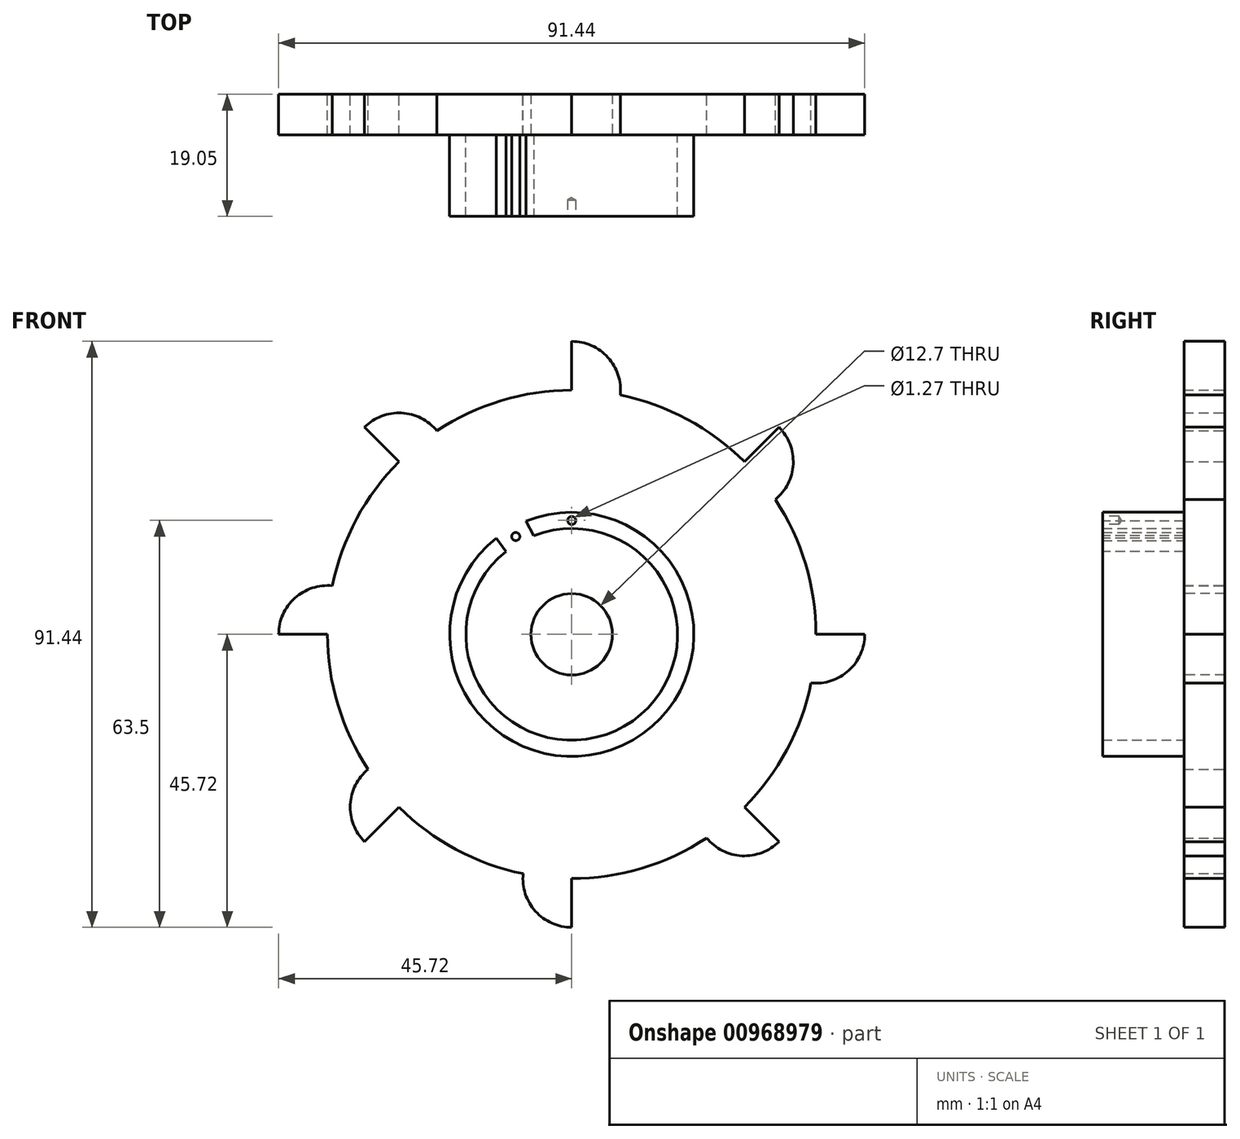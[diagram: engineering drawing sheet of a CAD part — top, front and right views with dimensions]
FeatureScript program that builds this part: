
annotation { "Feature Type Name" : "Feature", "Feature Type Description" : "" }
export const myFeature = defineFeature(function(context is Context, id is Id, definition is map)
    precondition{}
    {
        {
            var Q0;
            Q0=qCreatedBy(makeId("Front.planeOp"),FACE);
            var sketch = newSketch(context, id + "F0", { "sketchPlane" : qUnion([Q0])});
            skCircle(sketch, "E0", {"center": v(0, 0) * mm, "radius": 38.1 * mm});
            skLineSegment(sketch, "E1", {"start": v(0, 0) * mm, "end": v(0, 38.1) * mm});
            skLineSegment(sketch, "E2", {"start": v(0, 38.1) * mm, "end": v(0, 45.72) * mm});
            skArc(sketch, "E3", {"start": v(0, 45.72) * mm, "mid": v(5.65, 43.21) * mm, "end": v(7.58, 37.34) * mm});
            skArc(sketch, "E4.1.0", {"start": v(-32.33, 32.33) * mm, "mid": v(-26.56, 34.55) * mm, "end": v(-21.04, 31.76) * mm});
            skLineSegment(sketch, "E4.1.1", {"start": v(-26.94, 26.94) * mm, "end": v(-32.33, 32.33) * mm});
            skArc(sketch, "E4.2.0", {"start": v(-45.72, 0) * mm, "mid": v(-43.21, 5.65) * mm, "end": v(-37.34, 7.58) * mm});
            skLineSegment(sketch, "E4.2.1", {"start": v(-38.1, 0) * mm, "end": v(-45.72, 0) * mm});
            skArc(sketch, "E5.1.3.0", {"start": v(-32.33, -32.33) * mm, "mid": v(-34.55, -26.56) * mm, "end": v(-31.76, -21.04) * mm});
            skLineSegment(sketch, "E5.4.3.0", {"start": v(-26.94, -26.94) * mm, "end": v(-32.33, -32.33) * mm});
            skArc(sketch, "E6.1.4.0", {"start": v(0, -45.72) * mm, "mid": v(-5.65, -43.21) * mm, "end": v(-7.58, -37.34) * mm});
            skLineSegment(sketch, "E6.4.4.0", {"start": v(0, -38.1) * mm, "end": v(0, -45.72) * mm});
            skArc(sketch, "E6.1.5.0", {"start": v(32.33, -32.33) * mm, "mid": v(26.56, -34.55) * mm, "end": v(21.04, -31.76) * mm});
            skLineSegment(sketch, "E6.4.5.0", {"start": v(26.94, -26.94) * mm, "end": v(32.33, -32.33) * mm});
            skArc(sketch, "E7.1.6.0", {"start": v(45.72, 0) * mm, "mid": v(43.21, -5.65) * mm, "end": v(37.34, -7.58) * mm});
            skLineSegment(sketch, "E7.4.6.0", {"start": v(38.1, 0) * mm, "end": v(45.72, 0) * mm});
            skArc(sketch, "E7.1.7.0", {"start": v(32.33, 32.33) * mm, "mid": v(34.55, 26.56) * mm, "end": v(31.76, 21.04) * mm});
            skLineSegment(sketch, "E7.4.7.0", {"start": v(26.94, 26.94) * mm, "end": v(32.33, 32.33) * mm});
            skSolve(sketch);
        }
        {
            var Q0;
            Q0 = qSketchRegion(id + "F0", true);
            extrude(context, id + "F1", {"entities" : qUnion([Q0]), "depth" : 6.35 * mm, "offsetDistance" : 25.4 * mm});
        }
        {
            var Q0;
            Q0=makeQuery(id+"F1.opExtrude","CAP_FACE",FACE,{"disambiguationData":[OSD([sQuery(id+"F0.wireOp",EDGE,"E2"),sQuery(id+"F0.wireOp",EDGE,"E3"),sQuery(id+"F0.wireOp",EDGE,"E0"),sQuery(id+"F0.wireOp",EDGE,"E4.1.0"),sQuery(id+"F0.wireOp",EDGE,"E4.1.1"),sQuery(id+"F0.wireOp",EDGE,"E4.2.0"),sQuery(id+"F0.wireOp",EDGE,"E4.2.1"),sQuery(id+"F0.wireOp",EDGE,"E5.1.3.0"),sQuery(id+"F0.wireOp",EDGE,"E5.4.3.0"),sQuery(id+"F0.wireOp",EDGE,"E6.1.4.0"),sQuery(id+"F0.wireOp",EDGE,"E6.4.4.0"),sQuery(id+"F0.wireOp",EDGE,"E6.1.5.0"),sQuery(id+"F0.wireOp",EDGE,"E6.4.5.0"),sQuery(id+"F0.wireOp",EDGE,"E7.1.6.0"),sQuery(id+"F0.wireOp",EDGE,"E7.4.6.0"),sQuery(id+"F0.wireOp",EDGE,"E7.1.7.0"),sQuery(id+"F0.wireOp",EDGE,"E7.4.7.0")])],"isStart":false});
            var sketch = newSketch(context, id + "F2", { "sketchPlane" : qUnion([Q0])});
            skCircle(sketch, "E8", {"center": v(0, 0) * mm, "radius": 6.35 * mm});
            skSolve(sketch);
        }
        {
            var Q0;
            Q0=makeQuery(id+"F2.imprint","IMPRINT",FACE,{"disambiguationData":[TD([[makeQuery(id+"F2.imprint","IMPRINT",EDGE,{"derivedFrom":sQuery(id+"F2.wireOp",EDGE,"E8")}),1.0]])]});
            extrude(context, id + "F3", {"entities" : qUnion([Q0]), "operationType" : NewBodyOperationType.REMOVE, "oppositeDirection" : true, "depth" : 25.4 * mm, "offsetDistance" : 25.4 * mm});
        }
        {
            var Q0;
            Q0=makeQuery(id+"F1.opExtrude","CAP_FACE",FACE,{"disambiguationData":[OSD([sQuery(id+"F0.wireOp",EDGE,"E2"),sQuery(id+"F0.wireOp",EDGE,"E3"),sQuery(id+"F0.wireOp",EDGE,"E0"),sQuery(id+"F0.wireOp",EDGE,"E4.1.0"),sQuery(id+"F0.wireOp",EDGE,"E4.1.1"),sQuery(id+"F0.wireOp",EDGE,"E4.2.0"),sQuery(id+"F0.wireOp",EDGE,"E4.2.1"),sQuery(id+"F0.wireOp",EDGE,"E5.1.3.0"),sQuery(id+"F0.wireOp",EDGE,"E5.4.3.0"),sQuery(id+"F0.wireOp",EDGE,"E6.1.4.0"),sQuery(id+"F0.wireOp",EDGE,"E6.4.4.0"),sQuery(id+"F0.wireOp",EDGE,"E6.1.5.0"),sQuery(id+"F0.wireOp",EDGE,"E6.4.5.0"),sQuery(id+"F0.wireOp",EDGE,"E7.1.6.0"),sQuery(id+"F0.wireOp",EDGE,"E7.4.6.0"),sQuery(id+"F0.wireOp",EDGE,"E7.1.7.0"),sQuery(id+"F0.wireOp",EDGE,"E7.4.7.0")])],"isStart":false});
            var sketch = newSketch(context, id + "F4", { "sketchPlane" : qUnion([Q0])});
            skCircle(sketch, "E9", {"center": v(0, 0) * mm, "radius": 19.05 * mm});
            skCircle(sketch, "E10", {"center": v(0, 0) * mm, "radius": 16.51 * mm});
            skSolve(sketch);
        }
        {
            var Q0;
            Q0=makeQuery(id+"F4.imprint","IMPRINT",FACE,{"disambiguationData":[TD([[makeQuery(id+"F4.imprint","IMPRINT",EDGE,{"derivedFrom":sQuery(id+"F4.wireOp",EDGE,"E9")}),1.0]])]});
            extrude(context, id + "F5", {"entities" : qUnion([Q0]), "operationType" : NewBodyOperationType.ADD, "depth" : 12.7 * mm, "offsetDistance" : 25.4 * mm});
        }
        {
            var Q0;
            Q0=makeQuery(id+"F5.opExtrude","CAP_FACE",FACE,{"disambiguationData":[OSD([sQuery(id+"F4.wireOp",EDGE,"E9"),sQuery(id+"F4.wireOp",EDGE,"E10")])],"isStart":false});
            var sketch = newSketch(context, id + "F6", { "sketchPlane" : qUnion([Q0])});
            skArc(sketch, "E11", {"start": v(-7.15, 17.66) * mm, "mid": v(-9.54, 16.49) * mm, "end": v(-11.75, 15) * mm});
            skArc(sketch, "E12", {"start": v(-5.93, 15.4) * mm, "mid": v(-8.19, 14.34) * mm, "end": v(-10.25, 12.94) * mm});
            skLineSegment(sketch, "E13", {"start": v(-11.75, 15) * mm, "end": v(-10.25, 12.94) * mm});
            skLineSegment(sketch, "E14", {"start": v(-7.15, 17.66) * mm, "end": v(-5.93, 15.4) * mm});
            skSolve(sketch);
        }
        {
            var Q0;
            Q0=makeQuery(id+"F6.imprint","IMPRINT",FACE,{"disambiguationData":[TD([[makeQuery(id+"F6.imprint","IMPRINT",EDGE,{"derivedFrom":sQuery(id+"F6.wireOp",EDGE,"E11")}),1.0]])]});
            extrude(context, id + "F7", {"entities" : qUnion([Q0]), "operationType" : NewBodyOperationType.REMOVE, "oppositeDirection" : true, "depth" : 12.7 * mm, "offsetDistance" : 25.4 * mm});
        }
        {
            var Q0;
            {var subQ0=sQuery(id+"F0.wireOp",EDGE,"E7.4.7.0");var subQ1=sQuery(id+"F0.wireOp",EDGE,"E7.1.7.0");var subQ2=sQuery(id+"F0.wireOp",EDGE,"E7.4.6.0");var subQ3=sQuery(id+"F0.wireOp",EDGE,"E7.1.6.0");var subQ4=sQuery(id+"F0.wireOp",EDGE,"E6.4.5.0");var subQ5=sQuery(id+"F0.wireOp",EDGE,"E6.1.5.0");var subQ6=sQuery(id+"F0.wireOp",EDGE,"E6.4.4.0");var subQ7=sQuery(id+"F0.wireOp",EDGE,"E6.1.4.0");var subQ8=sQuery(id+"F0.wireOp",EDGE,"E5.4.3.0");var subQ9=sQuery(id+"F0.wireOp",EDGE,"E5.1.3.0");var subQ10=sQuery(id+"F0.wireOp",EDGE,"E4.2.1");var subQ11=sQuery(id+"F0.wireOp",EDGE,"E4.2.0");var subQ12=sQuery(id+"F0.wireOp",EDGE,"E4.1.1");var subQ13=sQuery(id+"F0.wireOp",EDGE,"E4.1.0");var subQ14=sQuery(id+"F0.wireOp",EDGE,"E0");var subQ15=sQuery(id+"F0.wireOp",EDGE,"E3");var subQ16=sQuery(id+"F0.wireOp",EDGE,"E2");var subQ17=makeQuery(id+"F1.opExtrude","CAP_FACE",FACE,{"disambiguationData":[OSD([subQ16,subQ15,subQ14,subQ13,subQ12,subQ11,subQ10,subQ9,subQ8,subQ7,subQ6,subQ5,subQ4,subQ3,subQ2,subQ1,subQ0])],"isStart":false});Q0=makeQuery(id+"F7.boolean.opBoolean","MERGE",FACE,{"derivedFrom":[makeQuery(id+"F5.boolean.opBoolean","SPLIT",FACE,{"disambiguationData":[TD([makeQuery(id+"F1.opExtrude","SWEPT_FACE",FACE,{"disambiguationData":[OSD([subQ16])]})])],"derivedFrom":subQ17}),makeQuery(id+"F5.boolean.opBoolean","SPLIT",FACE,{"disambiguationData":[TD([makeQuery(id+"F3.boolean.opBoolean","COPY",FACE,{"derivedFrom":makeQuery(id+"F3.opExtrude","SWEPT_FACE",FACE,{"disambiguationData":[OSD([sQuery(id+"F2.wireOp",EDGE,"E8")])]})})])],"derivedFrom":subQ17})],"fromTools":[makeQuery(id+"F7.opExtrude","CAP_FACE",FACE,{"disambiguationData":[OSD([sQuery(id+"F6.wireOp",EDGE,"E11"),sQuery(id+"F6.wireOp",EDGE,"E12"),sQuery(id+"F6.wireOp",EDGE,"E13"),sQuery(id+"F6.wireOp",EDGE,"E14")])],"isStart":false})]});}
            var sketch = newSketch(context, id + "F8", { "sketchPlane" : qUnion([Q0])});
            skLineSegment(sketch, "E15", {"start": v(-11.75, 15) * mm, "end": v(-7.15, 17.66) * mm});
            skLineSegment(sketch, "E16", {"start": v(-10.25, 12.94) * mm, "end": v(-5.93, 15.4) * mm});
            skCircle(sketch, "E17", {"center": v(-8.74, 15.27) * mm, "radius": 0.64 * mm});
            skSolve(sketch);
        }
        {
            var Q0;
            {var subQ0=sQuery(id+"F8.wireOp",EDGE,"E17");var subQ1=makeQuery(id+"F8.imprint","INTERSECT",VERTEX,{"derivedFrom":[sQuery(id+"F8.wireOp",EDGE,"E15"),subQ0]});Q0=makeQuery(id+"F8.imprint","IMPRINT",FACE,{"disambiguationData":[TD([[makeQuery(id+"F8.imprint","IMPRINT",EDGE,{"disambiguationData":[TD([[subQ1,-1.0]])],"derivedFrom":subQ0}),1.0]])]});}
            extrude(context, id + "F9", {"entities" : qUnion([Q0]), "operationType" : NewBodyOperationType.ADD, "depth" : 12.7 * mm, "offsetDistance" : 25.4 * mm});
        }
        {
            var Q0;
            Q0=makeQuery(id+"F5.opExtrude","CAP_FACE",FACE,{"disambiguationData":[OSD([sQuery(id+"F4.wireOp",EDGE,"E9"),sQuery(id+"F4.wireOp",EDGE,"E10")])],"isStart":false});
            var sketch = newSketch(context, id + "F10", { "sketchPlane" : qUnion([Q0])});
            skPoint(sketch, "E18", {"position": v(0, 17.78) * mm});
            skSolve(sketch);
        }
        {
            var Q0;
            Q0=sQuery(id+"F10.wireOp",VERTEX,"E18");
            var Q1;
            Q1=makeQuery(id+"F1.opExtrude","SWEPT_BODY",BODY,{"disambiguationData":[OSD([sQuery(id+"F0.wireOp",EDGE,"E2"),sQuery(id+"F0.wireOp",EDGE,"E3"),sQuery(id+"F0.wireOp",EDGE,"E0"),sQuery(id+"F0.wireOp",EDGE,"E4.1.0"),sQuery(id+"F0.wireOp",EDGE,"E4.1.1"),sQuery(id+"F0.wireOp",EDGE,"E4.2.0"),sQuery(id+"F0.wireOp",EDGE,"E4.2.1"),sQuery(id+"F0.wireOp",EDGE,"E5.1.3.0"),sQuery(id+"F0.wireOp",EDGE,"E5.4.3.0"),sQuery(id+"F0.wireOp",EDGE,"E6.1.4.0"),sQuery(id+"F0.wireOp",EDGE,"E6.4.4.0"),sQuery(id+"F0.wireOp",EDGE,"E6.1.5.0"),sQuery(id+"F0.wireOp",EDGE,"E6.4.5.0"),sQuery(id+"F0.wireOp",EDGE,"E7.1.6.0"),sQuery(id+"F0.wireOp",EDGE,"E7.4.6.0"),sQuery(id+"F0.wireOp",EDGE,"E7.1.7.0"),sQuery(id+"F0.wireOp",EDGE,"E7.4.7.0")])]});
            hole(context, id + "F11", {"style" : HoleStyle.SIMPLE, "endStyle" : HoleEndStyle.BLIND, "holeDiameter" : 1.27 * mm, "majorDiameter" : 6.35 * mm, "holeDepth" : 2.54 * mm, "isTappedThrough" : true, "tappedDepth" : 12.7 * mm, "tapClearance" : 3, "locations" : qUnion([Q0]), "scope" : qUnion([Q1])});
        }
    });
